FCSTD DOCUMENT  (FreeCAD 0.19R24415 (Git))
Label: ttgo_micro-32
License: All rights reserved
LicenseURL: http://en.wikipedia.org/wiki/All_rights_reserved
objects: Sketcher::SketchObject×1, PartDesign::Body×1
note: 2 computed .brp shape members not serialized (recipe doc carries the construction recipe); baked Part::Feature solids carry a one-line shape summary decoded from their .brp

FEATURE [Sketcher::SketchObject] Sketch
  FullyConstrained = true
  MapMode = 5
  Support = -> [XY_Plane]
  sketch-geometry (24):
    g0: LineSegment StartX=-6.55 StartY=9.45 StartZ=0 EndX=6.55 EndY=9.45 EndZ=0
    g1: LineSegment StartX=6.55 StartY=9.45 StartZ=0 EndX=6.55 EndY=-9.45 EndZ=0
    g2: LineSegment StartX=6.55 StartY=-9.45 StartZ=0 EndX=-6.55 EndY=-9.45 EndZ=0
    g3: LineSegment StartX=-6.55 StartY=-9.45 StartZ=0 EndX=-6.55 EndY=9.45 EndZ=0
    g4: LineSegment StartX=-7.95 StartY=6.11 StartZ=0 EndX=-5.85 EndY=6.11 EndZ=0
    g5: LineSegment StartX=-5.85 StartY=6.11 StartZ=0 EndX=-5.85 EndY=-7.89 EndZ=0
    g6: LineSegment StartX=-5.85 StartY=-7.89 StartZ=0 EndX=-7.95 EndY=-7.89 EndZ=0
    g7: LineSegment StartX=-7.95 StartY=-7.89 StartZ=0 EndX=-7.95 EndY=6.11 EndZ=0
    g8: LineSegment StartX=5.85 StartY=6.11 StartZ=0 EndX=7.95 EndY=6.11 EndZ=0
    g9: LineSegment StartX=7.95 StartY=6.11 StartZ=0 EndX=7.95 EndY=-7.89 EndZ=0
    g10: LineSegment StartX=7.95 StartY=-7.89 StartZ=0 EndX=5.85 EndY=-7.89 EndZ=0
    g11: LineSegment StartX=5.85 StartY=-7.89 StartZ=0 EndX=5.85 EndY=6.11 EndZ=0
    g12: LineSegment StartX=-3.5 StartY=-8.75 StartZ=0 EndX=3.5 EndY=-8.75 EndZ=0
    g13: LineSegment StartX=3.5 StartY=-8.75 StartZ=0 EndX=3.5 EndY=-10.85 EndZ=0
    g14: LineSegment StartX=3.5 StartY=-10.85 StartZ=0 EndX=-3.5 EndY=-10.85 EndZ=0
    g15: LineSegment StartX=-3.5 StartY=-10.85 StartZ=0 EndX=-3.5 EndY=-8.75 EndZ=0
    g16: GeomPoint X=-6.9 Y=-0.89 Z=0
    g17: GeomPoint X=6.9 Y=-0.89 Z=0
    g18: GeomPoint X=-1e-16 Y=-9.8 Z=0
    g19: LineSegment StartX=-2.65 StartY=-0.25 StartZ=0 EndX=2.65 EndY=-0.25 EndZ=0
    g20: LineSegment StartX=2.65 StartY=-0.25 StartZ=0 EndX=2.65 EndY=-5.55 EndZ=0
    g21: LineSegment StartX=2.65 StartY=-5.55 StartZ=0 EndX=-2.65 EndY=-5.55 EndZ=0
    g22: LineSegment StartX=-2.65 StartY=-5.55 StartZ=0 EndX=-2.65 EndY=-0.25 EndZ=0
    g23: GeomPoint X=1e-16 Y=-2.9 Z=0
  constraints (63):
    c: Coincident(g0,g1)
    c: Coincident(g1,g2)
    c: Coincident(g2,g3)
    c: Coincident(g3,g0)
    c: Horizontal(g0)
    c: Horizontal(g2)
    c: Vertical(g1)
    c: Vertical(g3)
    c: DistanceX(g0,g0) = 13.1
    c: DistanceY(g3,g3) = 18.9
    c: Symmetric(g0,g2,g-1)
    c: Coincident(g4,g5)
    c: Coincident(g5,g6)
    c: Coincident(g6,g7)
    c: Coincident(g7,g4)
    c: Horizontal(g4)
    c: Horizontal(g6)
    c: Vertical(g5)
    c: Vertical(g7)
    c: DistanceY(g7,g7) = 14
    c: DistanceY(g2,g6) = 1.56
    c: DistanceX(g4,g4) = 2.1
    c: DistanceX(g2,g5) = 0.7
    c: Coincident(g8,g9)
    c: Coincident(g9,g10)
    c: Coincident(g10,g11)
    c: Coincident(g11,g8)
    c: Symmetric(g4,g8,g-2)
    c: Symmetric(g4,g8,g-2)
    c: Symmetric(g6,g9,g-2)
    c: Symmetric(g5,g10,g-2)
    c: Coincident(g12,g13)
    c: Coincident(g13,g14)
    c: Coincident(g14,g15)
    c: Coincident(g15,g12)
    c: Horizontal(g12)
    c: Vertical(g13)
    c: Vertical(g15)
    c: DistanceX(g14,g14) = 7
    c: Symmetric(g13,g14,g-2)
    c: DistanceY(g13,g13) = 2.1
    c: DistanceY(g1,g12) = 0.7
    c: DistanceY(g5,g-1) = 7.89
    c: Symmetric(g16,g17,g-2)
    c: Symmetric(g4,g6,g16)
    c: DistanceX(g16,g-1) = 6.9
    c: Symmetric(g12,g13,g18)
    c: DistanceX(g12,g-1) = 3.5
    c: DistanceY(g18,g-1) = 9.8
    c: Coincident(g19,g20)
    c: Coincident(g20,g21)
    c: Coincident(g21,g22)
    c: Coincident(g22,g19)
    c: Horizontal(g21)
    c: Vertical(g20)
    c: Vertical(g22)
    c: DistanceX(g19,g19) = 5.3
    c: Equal(g20,g19)
    c: Symmetric(g19,g19,g-2)
    c: DistanceX(g19,g0) = 3.9
    c: DistanceY(g1,g20) = 3.9
    c: Symmetric(g19,g21,g23)
    c: DistanceY(g23,g-1) = 2.9
FEATURE [PartDesign::Body] Body
  Group = -> [Sketch]
  Origin = -> Origin
